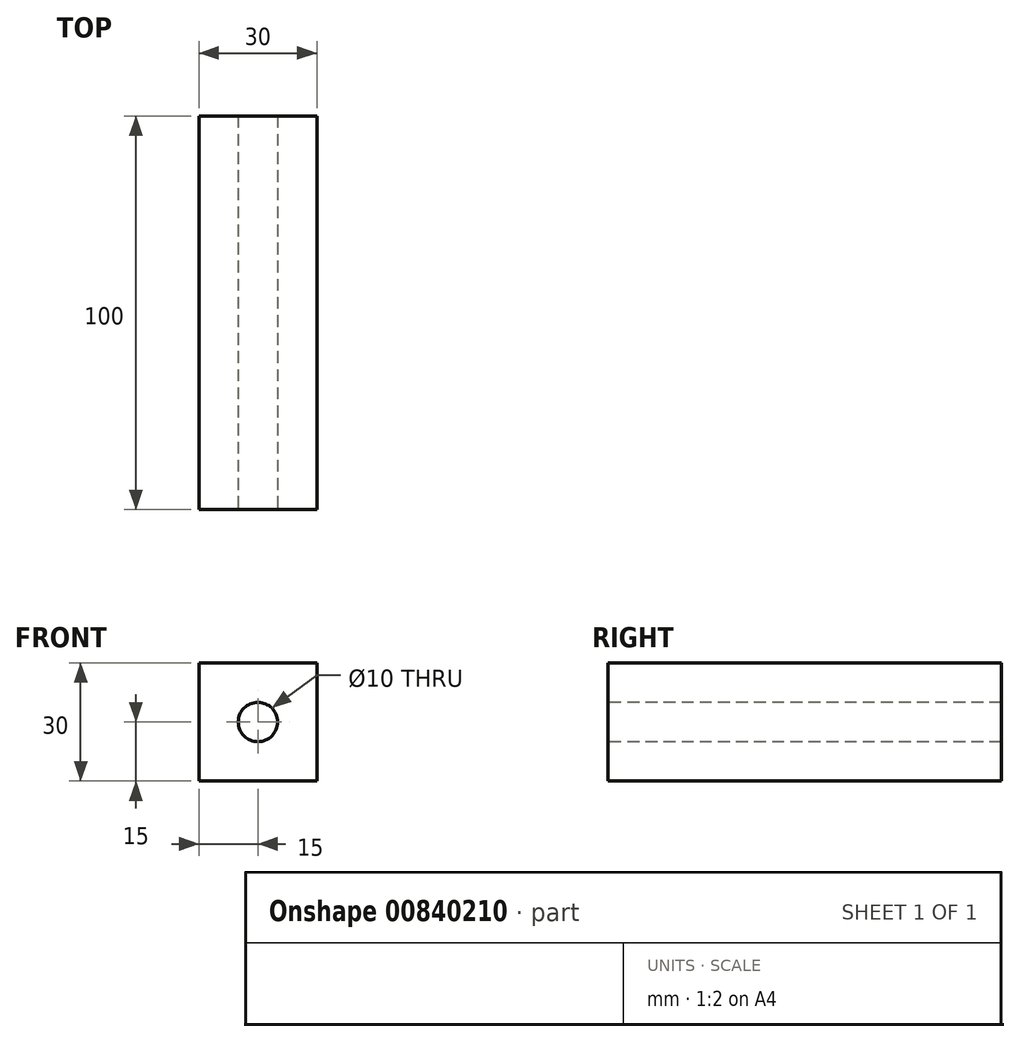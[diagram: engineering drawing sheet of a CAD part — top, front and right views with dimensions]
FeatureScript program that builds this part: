
annotation { "Feature Type Name" : "Feature", "Feature Type Description" : "" }
export const myFeature = defineFeature(function(context is Context, id is Id, definition is map)
    precondition{}
    {
        {
            var Q0;
            Q0=qCreatedBy(makeId("Front.planeOp"),FACE);
            var sketch = newSketch(context, id + "F0", { "sketchPlane" : qUnion([Q0])});
            skLineSegment(sketch, "E0.bottom", {"start": v(-15, 15) * mm, "end": v(15, 15) * mm});
            skLineSegment(sketch, "E0.top", {"start": v(-15, -15) * mm, "end": v(15, -15) * mm});
            skLineSegment(sketch, "E0.left", {"start": v(-15, 15) * mm, "end": v(-15, -15) * mm});
            skLineSegment(sketch, "E0.right", {"start": v(15, 15) * mm, "end": v(15, -15) * mm});
            skPoint(sketch, "E0.middle", {"position": v(0, 0) * mm});
            skSolve(sketch);
        }
        {
            var Q0;
            Q0=makeQuery(id+"F0.imprint","IMPRINT",FACE,{"disambiguationData":[TD([[makeQuery(id+"F0.imprint","IMPRINT",EDGE,{"derivedFrom":sQuery(id+"F0.wireOp",EDGE,"E0.bottom")}),-1.0]])]});
            extrude(context, id + "F1", {"entities" : qUnion([Q0]), "endBound" : BoundingType.SYMMETRIC, "depth" : 100 * mm, "offsetDistance" : 25 * mm});
        }
        {
            var Q0;
            Q0=makeQuery(id+"F1.opExtrude","CAP_FACE",FACE,{"disambiguationData":[OSD([sQuery(id+"F0.wireOp",EDGE,"E0.bottom"),sQuery(id+"F0.wireOp",EDGE,"E0.top"),sQuery(id+"F0.wireOp",EDGE,"E0.left"),sQuery(id+"F0.wireOp",EDGE,"E0.right")])],"isStart":false});
            var sketch = newSketch(context, id + "F2", { "sketchPlane" : qUnion([Q0])});
            skCircle(sketch, "E1", {"center": v(0, 0) * mm, "radius": 5 * mm});
            skSolve(sketch);
        }
        {
            var Q0;
            Q0=makeQuery(id+"F2.imprint","IMPRINT",FACE,{"disambiguationData":[TD([[makeQuery(id+"F2.imprint","IMPRINT",EDGE,{"derivedFrom":sQuery(id+"F2.wireOp",EDGE,"E1")}),1.0]])]});
            extrude(context, id + "F3", {"entities" : qUnion([Q0]), "operationType" : NewBodyOperationType.REMOVE, "oppositeDirection" : true, "depth" : 110 * mm, "offsetDistance" : 25 * mm});
        }
    });
